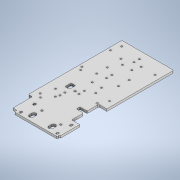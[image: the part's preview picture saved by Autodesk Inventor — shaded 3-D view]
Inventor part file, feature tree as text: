
AUTODESK INVENTOR PART (.ipt)
format: ipt  version: 2021 (Build 250183000, 183)  size: 407,552 bytes
history: native  units: mm
features: sketch x18, hole x10, extrude x8, fillet x5, projected_geometry x1
ambient origin geometry x8: Origin, YZ Plane, XZ Plane, XY Plane, X Axis, Y Axis, Z Axis, Center Point
bodies: Solid1 (feature_tree)
feature tree (42):
  extrude  "Extrusion1"  Depth=107.2mm
  fillet  "Fillet1"  Radius=210.0mm
  hole  "Hole1"  [1 undecoded]
  extrude  "Extrusion2"  Depth=8.0mm
  extrude  "Extrusion3"  Depth=82.0mm
  fillet  "Fillet2"  Radius=31.0mm
  extrude  "Extrusion4"  Depth=90.01mm
  hole  "Hole2"  [1 undecoded]
  extrude  "Extrusion5"  Depth=1.0mm
  hole  "Hole3"  [1 undecoded]
  hole  "Hole5"  [1 undecoded]
  hole  "Hole6"  [1 undecoded]
  hole  "Hole7"  [1 undecoded]
  hole  "Hole8"  [1 undecoded]
  hole  "Hole9"  [1 undecoded]
  extrude  "Extrusion6"  Depth=2.0mm
  fillet  "Fillet5"  Radius=16.45mm
  extrude  "Extrusion7"  Depth=80.15mm
  fillet  "Fillet6"  Radius=3.0mm
  extrude  "Extrusion8"  Depth=9.5mm
  fillet  "Fillet7"  Radius=10.0mm
  hole  "Hole10"  [1 undecoded]
  hole  "Hole11"  [1 undecoded]
  sketch  "Sketch1"  dims[d4=9.0mm d5=107.2mm d6=210.0mm]
  sketch  "Sketch2"  dims[d7=262.0mm d8=5.0mm d9=0.0mm]
  sketch  "Sketch3"  dims[d10=2.0mm]
  sketch  "Sketch4"  dims[d13=3.8mm d14=6.0mm d15=4.0mm d16=2.0mm d17=90.0deg d18=8.0mm d19=20.594885mm d20=12.0mm]
  sketch  "Sketch5"  dims[d21=31.0mm d24=82.0mm d25=31.0mm]
  sketch  "Sketch6"  dims[d26=8.86mm d27=90.01mm]
  sketch  "Sketch7"  dims[d28=9.3mm d29=40.299554mm]
  projected_geometry  "Projected Loop1"
  sketch  "Sketch8"  dims[d30=39.859554mm d31=1.0mm]
  sketch  "Sketch10"  dims[d32=4.8mm d33=1.0mm d34=4.8mm]
  sketch  "Sketch11"  dims[d35=1.0mm d36=4.8mm d37=1.0mm d38=4.8mm]
  sketch  "Sketch12"  dims[d39=0.0mm d40=0.0mm d41=81.99882mm]
  sketch  "Sketch13"  dims[d42=0.166341mm d43=30.0mm]
  sketch  "Sketch14"  dims[d44=102.0mm d45=61.0mm]
  sketch  "Sketch15"  dims[d46=150.0mm d47=18.0mm]
  sketch  "Sketch16"  dims[d48=0.0mm d49=0.0mm d50=2.0mm d51=16.45mm]
  sketch  "Sketch17"  dims[d52=36.15mm d53=80.15mm d54=3.0mm]
  sketch  "Sketch18"  dims[d55=9.5mm d56=3.0mm d57=9.5mm d58=10.0mm d59=0.0mm]
  sketch  "Sketch19"  dims[d60=37.5mm d61=85.54mm d62=96.54mm d63=3.8mm d64=6.0mm d65=4.0mm d66=2.0mm d67=90.0deg d68=8.0mm d69=20.594885mm d71=2.5mm d72=0.0mm d74=27.0mm d75=21.12mm d76=33.092mm d77=69.429mm d80=109.55mm d81=108.02mm d82=21.56mm d83=69.82mm d84=4.5mm d85=6.0mm d86=4.0mm d87=2.0mm d88=90.0deg d89=8.0mm d90=20.594885mm d102=60.0mm d103=17.0mm d104=12.0mm d105=61.75mm d106=61.75mm d107=3.8mm d108=6.0mm d109=4.0mm d110=2.0mm d111=90.0deg d112=8.0mm d113=20.594885mm d114=128.5mm d115=60.0mm d116=12.0mm d117=12.0mm d118=3.8mm d119=6.0mm d120=4.0mm d121=2.0mm d122=90.0deg d123=8.0mm d124=20.594885mm d125=6.5mm d126=32.25mm d127=64.0mm d128=3.8mm d129=6.0mm d130=4.0mm d131=2.0mm d132=90.0deg d133=8.0mm d134=20.594885mm d135=19.5mm d136=168.5mm d137=34.0mm d138=3.8mm d139=6.0mm d140=4.0mm d141=2.0mm d142=90.0deg d143=8.0mm d144=20.594885mm d145=11.5mm d146=12.0mm d147=104.0mm d148=195.0mm d149=3.8mm d150=6.0mm d151=4.0mm d152=2.0mm d153=90.0deg d154=8.0mm d155=20.594885mm d156=10.0mm d157=14.0mm d158=26.0mm d159=140.0mm d160=0.0mm d161=0.0mm d162=2.0mm d163=9.0mm d164=6.0mm d165=2.0mm d166=6.0mm d167=0.0mm d168=0.0mm d169=2.0mm d170=8.0mm d171=30.5mm d172=34.0mm d173=0.0mm d174=0.0mm d175=2.0mm d176=81.5mm d177=37.0mm d178=147.0mm d179=3.8mm d180=6.0mm d181=4.0mm d182=2.0mm d183=90.0deg d184=8.0mm d185=20.594885mm d186=43.0mm d187=62.0mm d188=34.0mm d189=3.0mm d191=12.0mm d192=21.0mm d193=21.0mm d194=12.0mm d195=22.0mm d196=22.0mm d197=3.8mm d198=6.0mm d199=4.0mm d200=2.0mm d201=90.0deg d202=8.0mm d203=20.594885mm d204=22.0mm d205=22.0mm d206=47.0mm]
note: 10 required parameter values undecoded (feature->parameter linkage not recoverable at this tier; creation-order binding heuristic only, values carry confidence <= 0.55)
